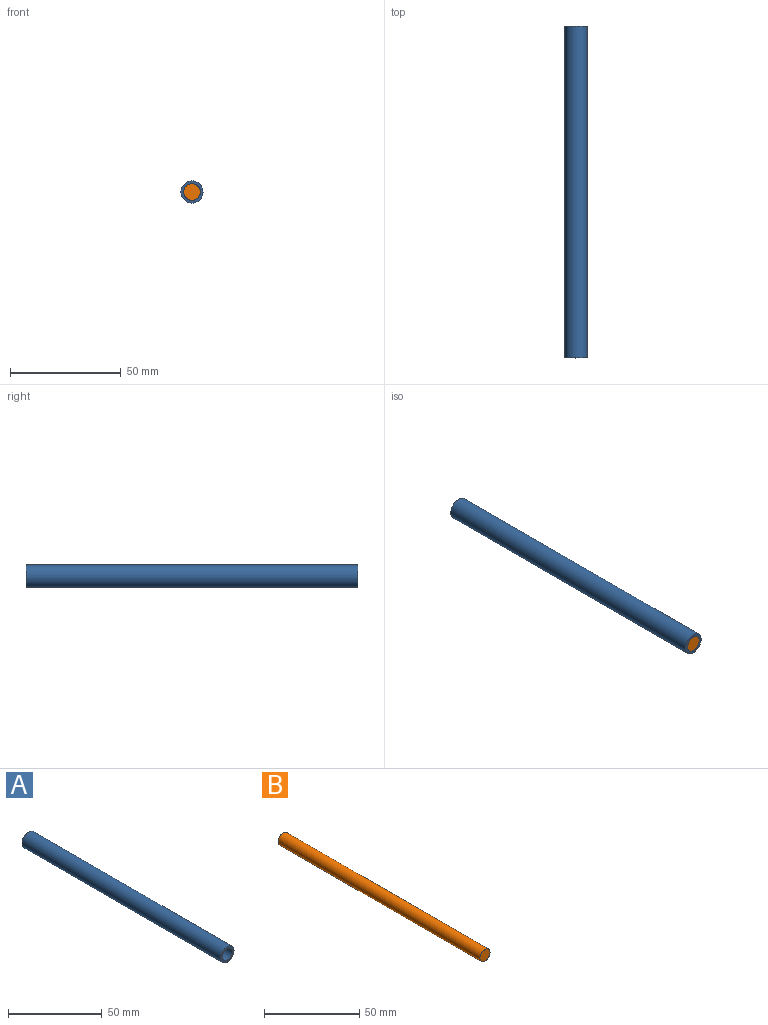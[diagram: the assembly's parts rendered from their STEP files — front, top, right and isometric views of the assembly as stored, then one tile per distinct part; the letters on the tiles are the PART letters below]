
ASSEMBLY  parts=2 mates=1
PART A: 4 faces, bbox 10x150x10 mm
  f0: cylinder r=5mm len=150mm, axis (0,-1,0), area 4712.4mm2, adj f1,f2
  f1: plane 10x10mm, normal (0,1,0), area 34.4mm2, adj f0,f3
  f2: plane 10x10mm, normal (0,-1,0), area 34.4mm2, adj f0,f3
  f3: cylinder r=3.75mm len=150mm, axis (0,-1,0), area 3534.3mm2, adj f1,f2
PART B: 3 faces, bbox 7.5x150x7.5 mm
  f0: cylinder r=3.75mm len=150mm, axis (0,-1,0), area 3534.3mm2, adj f1,f2
  f1: plane 7.5x7.5mm, normal (0,1,0), area 44.2mm2, adj f0
  f2: plane 7.5x7.5mm, normal (0,-1,0), area 44.2mm2, adj f0
PLACE A t=(10.24,-42.08,40.51)mm
PLACE B t=(10.24,-42.08,40.51)mm
MATE fastened B.f0 <-> A.f0  axis (0,-1,0) through (10.24,-42.08,40.51)mm
